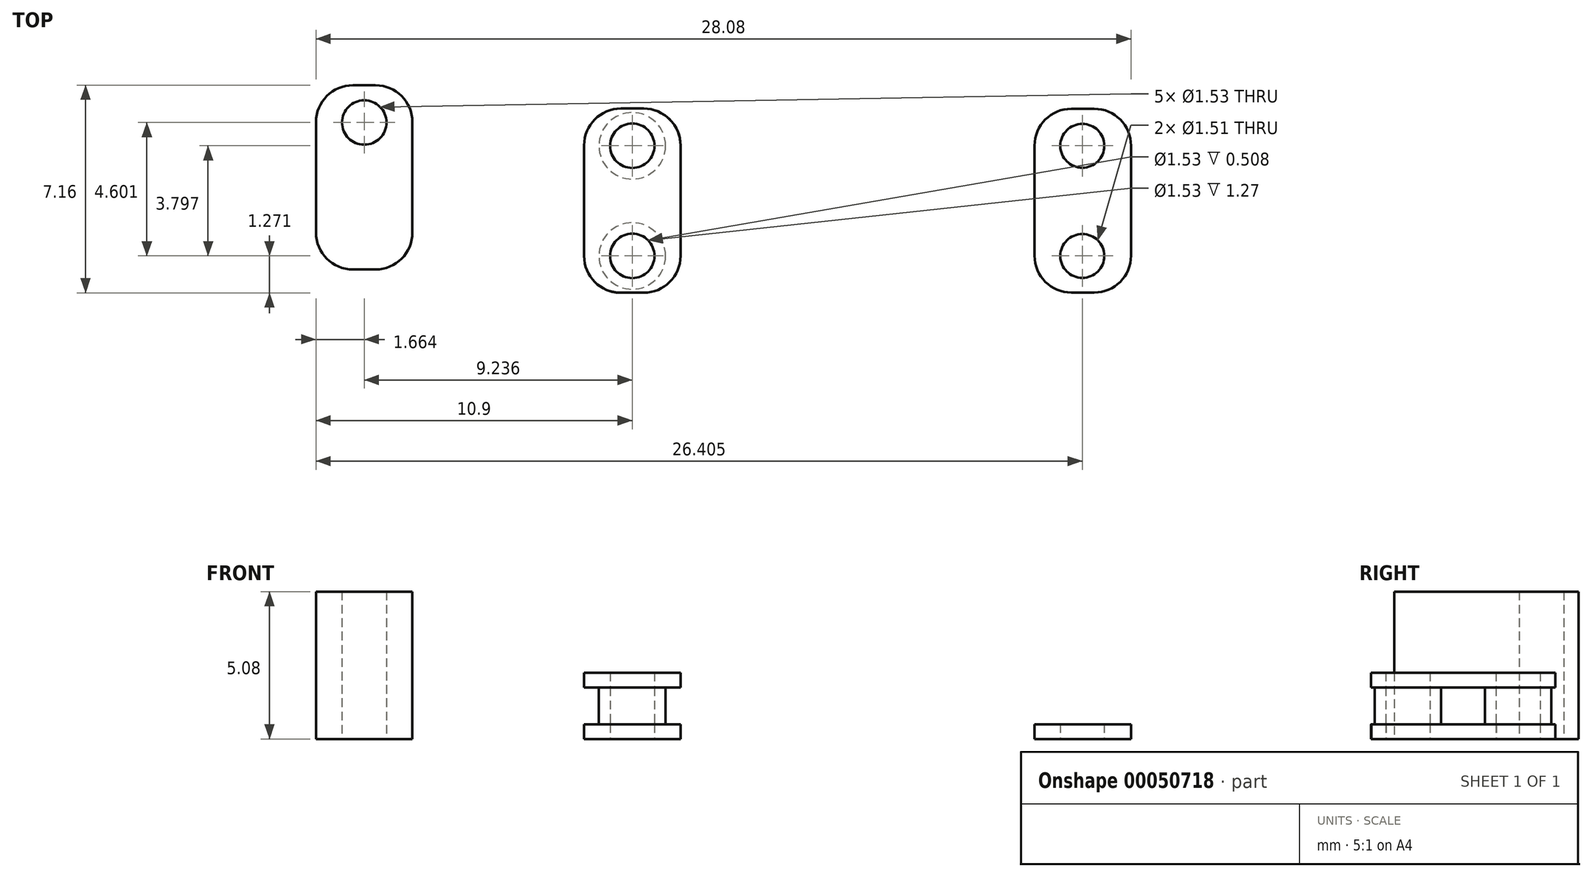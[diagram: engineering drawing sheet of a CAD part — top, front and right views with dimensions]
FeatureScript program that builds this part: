
annotation { "Feature Type Name" : "Feature", "Feature Type Description" : "" }
export const myFeature = defineFeature(function(context is Context, id is Id, definition is map)
    precondition{}
    {
        {
            var Q0;
            Q0=qCreatedBy(makeId("Top.planeOp"),FACE);
            var sketch = newSketch(context, id + "F0", { "sketchPlane" : qUnion([Q0])});
            skLineSegment(sketch, "E0", {"start": v(-1.66, 3.18) * mm, "end": v(-1.66, -3.17) * mm});
            skLineSegment(sketch, "E1", {"start": v(-1.66, -3.17) * mm, "end": v(1.66, -3.17) * mm});
            skLineSegment(sketch, "E2", {"start": v(1.66, -3.17) * mm, "end": v(1.66, 3.18) * mm});
            skLineSegment(sketch, "E3", {"start": v(-1.66, 3.18) * mm, "end": v(1.66, 3.18) * mm});
            skLineSegment(sketch, "E4", {"start": v(13.86, 3.17) * mm, "end": v(17.18, 3.17) * mm});
            skLineSegment(sketch, "E5", {"start": v(13.86, -3.16) * mm, "end": v(13.86, 3.17) * mm});
            skPoint(sketch, "E6.endSnap0", {"position": v(0, -3.17) * mm});
            skCircle(sketch, "E7", {"center": v(0, -1.9) * mm, "radius": 0.77 * mm});
            skCircle(sketch, "E8.MirrorC", {"center": v(0, 1.9) * mm, "radius": 0.77 * mm});
            skLineSegment(sketch, "E9", {"start": v(17.18, 3.17) * mm, "end": v(17.18, -3.16) * mm});
            skCircle(sketch, "E10", {"center": v(15.5, 1.9) * mm, "radius": 0.76 * mm});
            skCircle(sketch, "E11", {"center": v(15.5, -1.9) * mm, "radius": 0.76 * mm});
            skLineSegment(sketch, "E12", {"start": v(13.86, -3.16) * mm, "end": v(17.18, -3.16) * mm});
            skSolve(sketch);
        }
        {
            var Q0;
            Q0=makeQuery(id+"F0.imprint","IMPRINT",FACE,{"disambiguationData":[TD([[makeQuery(id+"F0.imprint","IMPRINT",EDGE,{"derivedFrom":sQuery(id+"F0.wireOp",EDGE,"E0")}),1.0]])]});
            extrude(context, id + "F1", {"entities" : qUnion([Q0]), "depth" : 0.5 * mm});
        }
        {
            var Q0;
            Q0=makeQuery(id+"F1.opExtrude","SWEPT_EDGE",EDGE,{"disambiguationData":[OSD([sQuery(id+"F0.wireOp",EDGE,"E0"),sQuery(id+"F0.wireOp",EDGE,"E1")])]});
            var Q1;
            Q1=makeQuery(id+"F1.opExtrude","SWEPT_EDGE",EDGE,{"disambiguationData":[OSD([sQuery(id+"F0.wireOp",EDGE,"E1"),sQuery(id+"F0.wireOp",EDGE,"E2")])]});
            var Q2;
            Q2=makeQuery(id+"F1.opExtrude","SWEPT_EDGE",EDGE,{"disambiguationData":[OSD([sQuery(id+"F0.wireOp",EDGE,"E0"),sQuery(id+"F0.wireOp",EDGE,"E3")])]});
            var Q3;
            Q3=makeQuery(id+"F1.opExtrude","SWEPT_EDGE",EDGE,{"disambiguationData":[OSD([sQuery(id+"F0.wireOp",EDGE,"E2"),sQuery(id+"F0.wireOp",EDGE,"E3")])]});
            fillet(context, id + "F2", {"entities" : qUnion([Q0, Q1, Q2, Q3]), "radius" : 1.27 * mm, "tangentPropagation" : true, "allowEdgeOverflow" : false});
        }
        {
            var Q0;
            Q0=makeQuery(id+"F0.imprint","IMPRINT",FACE,{"disambiguationData":[TD([[makeQuery(id+"F0.imprint","IMPRINT",EDGE,{"derivedFrom":sQuery(id+"F0.wireOp",EDGE,"E4")}),-1.0]])]});
            extrude(context, id + "F3", {"entities" : qUnion([Q0]), "depth" : 0.5 * mm});
        }
        {
            var Q0;
            Q0=makeQuery(id+"F3.opExtrude","SWEPT_EDGE",EDGE,{"disambiguationData":[OSD([sQuery(id+"F0.wireOp",EDGE,"E5"),sQuery(id+"F0.wireOp",EDGE,"E12")])]});
            var Q1;
            Q1=makeQuery(id+"F3.opExtrude","SWEPT_EDGE",EDGE,{"disambiguationData":[OSD([sQuery(id+"F0.wireOp",EDGE,"E9"),sQuery(id+"F0.wireOp",EDGE,"E12")])]});
            var Q2;
            Q2=makeQuery(id+"F3.opExtrude","SWEPT_EDGE",EDGE,{"disambiguationData":[OSD([sQuery(id+"F0.wireOp",EDGE,"E4"),sQuery(id+"F0.wireOp",EDGE,"E9")])]});
            var Q3;
            Q3=makeQuery(id+"F3.opExtrude","SWEPT_EDGE",EDGE,{"disambiguationData":[OSD([sQuery(id+"F0.wireOp",EDGE,"E4"),sQuery(id+"F0.wireOp",EDGE,"E5")])]});
            fillet(context, id + "F4", {"entities" : qUnion([Q0, Q1, Q2, Q3]), "radius" : 1.27 * mm, "tangentPropagation" : true, "allowEdgeOverflow" : false});
        }
        {
            var Q0;
            Q0=qCreatedBy(makeId("Top.planeOp"),FACE);
            var sketch = newSketch(context, id + "F5", { "sketchPlane" : qUnion([Q0])});
            skLineSegment(sketch, "E13", {"start": v(-10.9, 3.99) * mm, "end": v(-10.9, -2.36) * mm});
            skLineSegment(sketch, "E14", {"start": v(-10.9, -2.36) * mm, "end": v(-7.57, -2.36) * mm});
            skLineSegment(sketch, "E15", {"start": v(-7.57, -2.36) * mm, "end": v(-7.57, 3.99) * mm});
            skLineSegment(sketch, "E16", {"start": v(-10.9, 3.99) * mm, "end": v(-7.57, 3.99) * mm});
            skPoint(sketch, "E17.endSnap0", {"position": v(-9.24, -2.36) * mm});
            skCircle(sketch, "E18", {"center": v(-9.24, -1.1) * mm, "radius": 0.77 * mm});
            skCircle(sketch, "E19.MirrorC", {"center": v(-9.24, 2.7) * mm, "radius": 0.77 * mm});
            skSolve(sketch);
        }
        {
            var Q0;
            Q0=makeQuery(id+"F5.imprint","IMPRINT",FACE,{"disambiguationData":[TD([[makeQuery(id+"F5.imprint","IMPRINT",EDGE,{"derivedFrom":sQuery(id+"F5.wireOp",EDGE,"E13")}),1.0]])]});
            extrude(context, id + "F6", {"entities" : qUnion([Q0]), "depth" : 0.5 * mm});
        }
        {
            var Q0;
            Q0=makeQuery(id+"F5.imprint","IMPRINT",FACE,{"disambiguationData":[TD([[makeQuery(id+"F5.imprint","IMPRINT",EDGE,{"derivedFrom":sQuery(id+"F5.wireOp",EDGE,"E19.MirrorC")}),-1.0]])]});
            var Q1;
            Q1=makeQuery(id+"F5.imprint","IMPRINT",FACE,{"disambiguationData":[TD([[makeQuery(id+"F5.imprint","IMPRINT",EDGE,{"derivedFrom":sQuery(id+"F5.wireOp",EDGE,"E18")}),1.0]])]});
            extrude(context, id + "F7", {"entities" : qUnion([Q0, Q1]), "operationType" : NewBodyOperationType.ADD, "depth" : 5.08 * mm});
        }
        {
            var Q0;
            Q0=makeQuery(id+"F6.opExtrude","SWEPT_EDGE",EDGE,{"disambiguationData":[OSD([sQuery(id+"F5.wireOp",EDGE,"E13"),sQuery(id+"F5.wireOp",EDGE,"E16")])]});
            var Q1;
            Q1=makeQuery(id+"F6.opExtrude","SWEPT_EDGE",EDGE,{"disambiguationData":[OSD([sQuery(id+"F5.wireOp",EDGE,"E15"),sQuery(id+"F5.wireOp",EDGE,"E16")])]});
            var Q2;
            Q2=makeQuery(id+"F6.opExtrude","SWEPT_EDGE",EDGE,{"disambiguationData":[OSD([sQuery(id+"F5.wireOp",EDGE,"E13"),sQuery(id+"F5.wireOp",EDGE,"E14")])]});
            var Q3;
            Q3=makeQuery(id+"F6.opExtrude","SWEPT_EDGE",EDGE,{"disambiguationData":[OSD([sQuery(id+"F5.wireOp",EDGE,"E14"),sQuery(id+"F5.wireOp",EDGE,"E15")])]});
            fillet(context, id + "F8", {"entities" : qUnion([Q0, Q1, Q2, Q3]), "radius" : 1.27 * mm, "tangentPropagation" : true, "allowEdgeOverflow" : false});
        }
        {
            var Q0;
            Q0=makeQuery(id+"F1.opExtrude","CAP_FACE",FACE,{"disambiguationData":[OSD([sQuery(id+"F0.wireOp",EDGE,"E0"),sQuery(id+"F0.wireOp",EDGE,"E1"),sQuery(id+"F0.wireOp",EDGE,"E2"),sQuery(id+"F0.wireOp",EDGE,"E3"),sQuery(id+"F0.wireOp",EDGE,"E7"),sQuery(id+"F0.wireOp",EDGE,"E8.MirrorC")])],"isStart":false});
            var sketch = newSketch(context, id + "F9", { "sketchPlane" : qUnion([Q0])});
            skCircle(sketch, "E20", {"center": v(0, 1.9) * mm, "radius": 0.76 * mm});
            skCircle(sketch, "E21", {"center": v(0, 1.9) * mm, "radius": 1.15 * mm});
            skLineSegment(sketch, "E22", {"start": v(-1.03, 0) * mm, "end": v(1.46, 0) * mm});
            skCircle(sketch, "E23.MirrorC", {"center": v(0, -1.9) * mm, "radius": 1.15 * mm});
            skCircle(sketch, "E24.MirrorC", {"center": v(0, -1.9) * mm, "radius": 0.76 * mm});
            skSolve(sketch);
        }
        {
            var Q0;
            Q0 = qSketchRegion(id + "F9", true);
            extrude(context, id + "F10", {"entities" : qUnion([Q0]), "operationType" : NewBodyOperationType.ADD, "depth" : 1.27 * mm});
        }
        {
            var Q0;
            Q0=qCreatedBy(makeId("Top.planeOp"),FACE);
            cPlane(context, id + "F11", {"entities" : qUnion([Q0]), "cplaneType" : CPlaneType.OFFSET, "offset" : 1.78 * mm, "width" : 152.4 * mm, "height" : 152.4 * mm});
        }
        {
            var Q0;
            Q0=qCreatedBy(id+"F11.planeOp",FACE);
            var sketch = newSketch(context, id + "F12", { "sketchPlane" : qUnion([Q0])});
            skLineSegment(sketch, "E25", {"start": v(-1.66, 3.18) * mm, "end": v(-1.66, -3.17) * mm});
            skLineSegment(sketch, "E26", {"start": v(-1.66, -3.17) * mm, "end": v(1.66, -3.17) * mm});
            skLineSegment(sketch, "E27", {"start": v(1.66, -3.17) * mm, "end": v(1.66, 3.18) * mm});
            skLineSegment(sketch, "E28", {"start": v(-1.66, 3.18) * mm, "end": v(1.66, 3.18) * mm});
            skCircle(sketch, "E29", {"center": v(0, -1.9) * mm, "radius": 0.77 * mm});
            skCircle(sketch, "E30.MirrorC", {"center": v(0, 1.9) * mm, "radius": 0.77 * mm});
            skSolve(sketch);
        }
        {
            var Q0;
            Q0 = qSketchRegion(id + "F12", true);
            extrude(context, id + "F13", {"entities" : qUnion([Q0]), "operationType" : NewBodyOperationType.ADD, "depth" : 0.5 * mm});
        }
        {
            var Q0;
            Q0=makeQuery(id+"F13.opExtrude","SWEPT_EDGE",EDGE,{"disambiguationData":[OSD([sQuery(id+"F12.wireOp",EDGE,"E25"),sQuery(id+"F12.wireOp",EDGE,"E26")])]});
            var Q1;
            Q1=makeQuery(id+"F13.opExtrude","SWEPT_EDGE",EDGE,{"disambiguationData":[OSD([sQuery(id+"F12.wireOp",EDGE,"E26"),sQuery(id+"F12.wireOp",EDGE,"E27")])]});
            var Q2;
            Q2=makeQuery(id+"F13.opExtrude","SWEPT_EDGE",EDGE,{"disambiguationData":[OSD([sQuery(id+"F12.wireOp",EDGE,"E27"),sQuery(id+"F12.wireOp",EDGE,"E28")])]});
            var Q3;
            Q3=makeQuery(id+"F13.opExtrude","SWEPT_EDGE",EDGE,{"disambiguationData":[OSD([sQuery(id+"F12.wireOp",EDGE,"E25"),sQuery(id+"F12.wireOp",EDGE,"E28")])]});
            fillet(context, id + "F14", {"entities" : qUnion([Q0, Q1, Q2, Q3]), "radius" : 1.27 * mm, "tangentPropagation" : true, "allowEdgeOverflow" : false});
        }
    });
